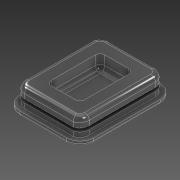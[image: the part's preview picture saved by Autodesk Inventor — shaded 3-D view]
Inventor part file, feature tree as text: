
AUTODESK INVENTOR PART (.ipt)
format: ipt  version: 2021 (Build 250183000, 183)  size: 365,056 bytes
history: native  units: mm
features: extrude x6, sketch x5, fillet x3, projected_geometry x3, other x1
ambient origin geometry x8: Origin, YZ Plane, XZ Plane, XY Plane, X Axis, Y Axis, Z Axis, Center Point
bodies: Body1 (feature_tree)
feature tree (18):
  other  "Sólido1"
  sketch  "Boceto1"  dims[d0=27.85mm d1=40.5mm]
  extrude  "Extrusión1"  Depth=40.5mm
  extrude  "Extrusión2"  Depth=2.0mm
  extrude  "Extrusión3"  Depth=2.0mm
  extrude  "Extrusión4"  Depth=2.0mm
  extrude  "Extrusión5"  Depth=4.0mm TaperAngle=0.0deg
  fillet  "Empalme1"  Radius=2.0mm
  fillet  "Empalme2"  Radius=1.8mm
  fillet  "Empalme3"  Radius=1.5mm
  extrude  "Extrusión6"  Depth=4.0mm TaperAngle=0.0deg
  sketch  "Boceto2"  dims[d2=6.0mm d3=2.0mm]
  projected_geometry  "Contorno proyectado1"
  sketch  "Boceto3"  dims[d4=2.0mm d5=2.0mm]
  projected_geometry  "Contorno proyectado2"
  sketch  "Boceto4"  dims[d6=2.0mm d7=2.0mm]
  projected_geometry  "Contorno proyectado3"
  sketch  "Boceto5"  dims[d8=0.4mm d9=4.0mm d10=0.0mm d11=2.0mm d12=0.0mm d13=1.8mm d14=1.5mm d15=0.0mm d16=4.0mm d17=0.0mm d18=1.8mm d19=2.0mm d20=6.0mm d21=0.0mm d22=2.0mm d23=2.0mm d24=1.0mm d25=0.3mm d26=0.0mm d27=0.5mm d28=0.872665mm]
